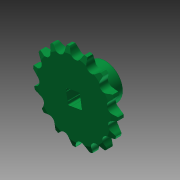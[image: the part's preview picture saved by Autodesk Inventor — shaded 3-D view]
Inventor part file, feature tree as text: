
AUTODESK INVENTOR PART (.ipt)
format: ipt  version: 2014 SP1 (Build 180222100, 222)  size: 683,520 bytes
history: native  units: in
note: dims shown in document units (in); Inventor stores cm internally (conversion verified against a paired STEP export)
features: other x1, imported_body x1, extrude x1, sketch x1
ambient origin geometry x8: Origin, YZ Plane, XZ Plane, XY Plane, X Axis, Y Axis, Z Axis, Center Point
bodies: Body1 (feature_tree)
feature tree (4):
  parser-record x1  (decoder bookkeeping rows leaked as tree rows — omitted from the tree; the rows remain in map.json)
  imported_body  "Base1"
  extrude  "Extrusion1"  [1 undecoded]
  sketch  "Sketch1"  dims[d0=1.0in d1=0.0in]
note: 1 required parameter value undecoded (feature->parameter linkage not recoverable at this tier; creation-order binding heuristic only, values carry confidence <= 0.55)
